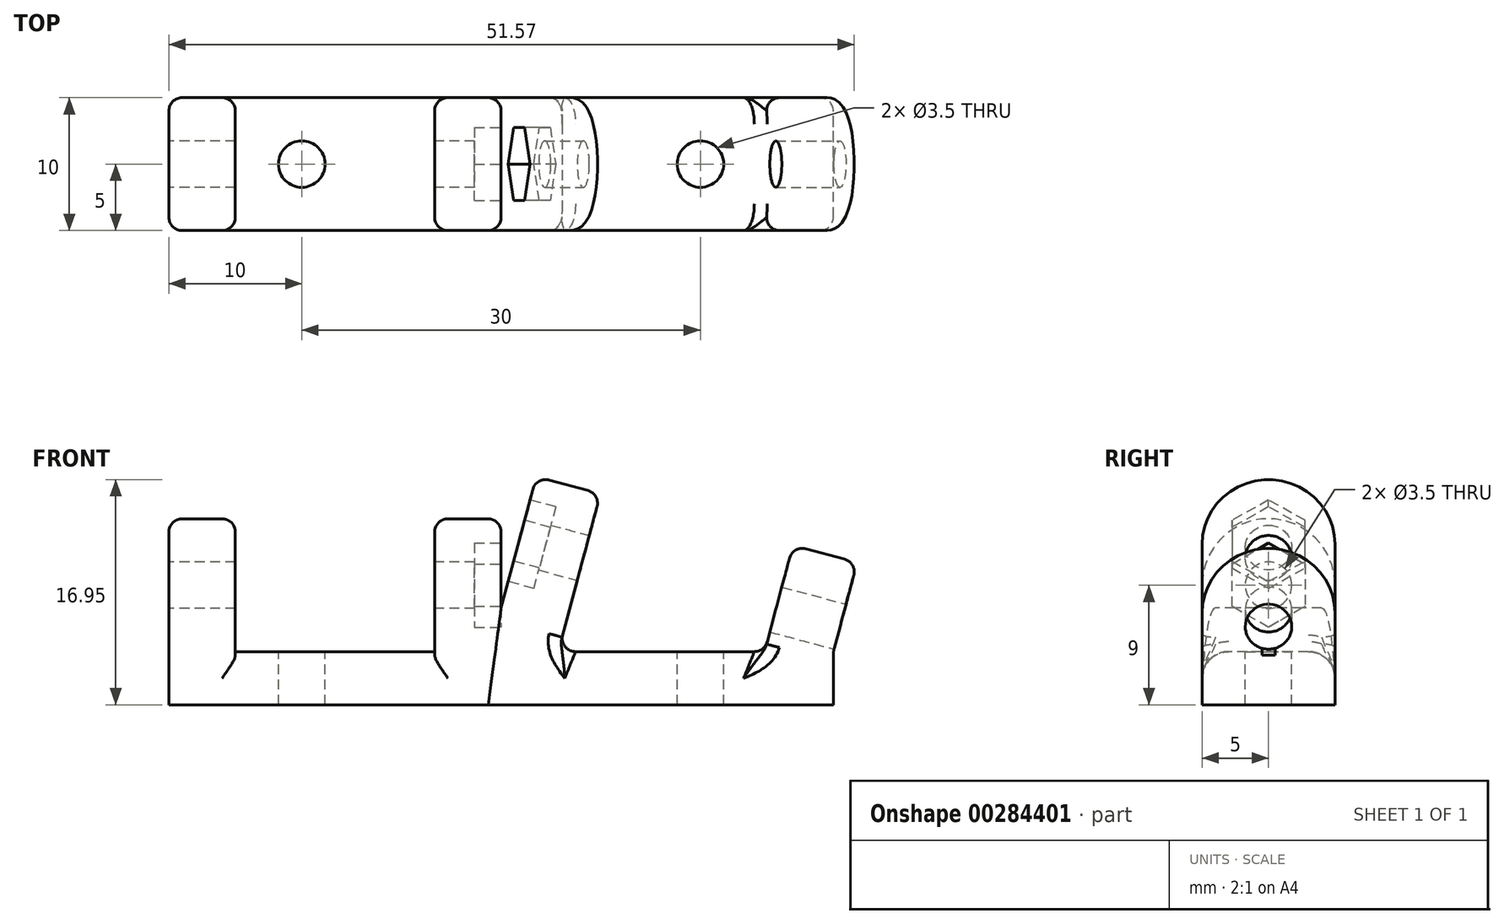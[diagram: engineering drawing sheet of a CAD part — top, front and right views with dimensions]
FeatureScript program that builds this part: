
annotation { "Feature Type Name" : "Feature", "Feature Type Description" : "" }
export const myFeature = defineFeature(function(context is Context, id is Id, definition is map)
    precondition{}
    {
        {
            var Q0;
            Q0=qCreatedBy(makeId("Top.planeOp"),FACE);
            var sketch = newSketch(context, id + "F0", { "sketchPlane" : qUnion([Q0])});
            skLineSegment(sketch, "E0.bottom", {"start": v(0, 0) * mm, "end": v(50, 0) * mm});
            skLineSegment(sketch, "E0.top", {"start": v(0, 10) * mm, "end": v(50, 10) * mm});
            skLineSegment(sketch, "E0.left", {"start": v(0, 0) * mm, "end": v(0, 10) * mm});
            skLineSegment(sketch, "E0.right", {"start": v(50, 0) * mm, "end": v(50, 10) * mm});
            skSolve(sketch);
        }
        {
            var Q0;
            Q0 = qSketchRegion(id + "F0", true);
            extrude(context, id + "F1", {"entities" : qUnion([Q0]), "depth" : 4 * mm});
        }
        {
            var Q0;
            Q0=makeQuery(id+"F1.opExtrude","SWEPT_FACE",FACE,{"disambiguationData":[OSD([sQuery(id+"F0.wireOp",EDGE,"E0.bottom")])]});
            var sketch = newSketch(context, id + "F2", { "sketchPlane" : qUnion([Q0])});
            skLineSegment(sketch, "E1", {"start": v(0, 4) * mm, "end": v(0, 14) * mm});
            skLineSegment(sketch, "E2", {"start": v(0, 14) * mm, "end": v(5, 14) * mm});
            skLineSegment(sketch, "E3", {"start": v(5, 14) * mm, "end": v(5, 4) * mm});
            skLineSegment(sketch, "E4", {"start": v(5, 4) * mm, "end": v(0, 4) * mm});
            skLineSegment(sketch, "E5", {"start": v(20, 4) * mm, "end": v(20, 14) * mm});
            skLineSegment(sketch, "E6", {"start": v(20, 14) * mm, "end": v(25, 14) * mm});
            skLineSegment(sketch, "E7", {"start": v(25, 14) * mm, "end": v(25, 7.3) * mm});
            skLineSegment(sketch, "E8", {"start": v(25, 4) * mm, "end": v(20, 4) * mm});
            skLineSegment(sketch, "E9", {"start": v(25, 7.3) * mm, "end": v(27.65, 17.18) * mm});
            skLineSegment(sketch, "E10", {"start": v(27.65, 17.18) * mm, "end": v(32.48, 15.88) * mm});
            skLineSegment(sketch, "E11", {"start": v(32.48, 15.88) * mm, "end": v(29.3, 4) * mm});
            skLineSegment(sketch, "E12", {"start": v(25, 4) * mm, "end": v(29.3, 4) * mm});
            skLineSegment(sketch, "E13", {"start": v(44.82, 4) * mm, "end": v(46.97, 12) * mm});
            skLineSegment(sketch, "E14", {"start": v(46.97, 12) * mm, "end": v(51.8, 10.7) * mm});
            skLineSegment(sketch, "E15", {"start": v(51.8, 10.7) * mm, "end": v(50, 4) * mm});
            skLineSegment(sketch, "E16", {"start": v(50, 4) * mm, "end": v(44.82, 4) * mm});
            skLineSegment(sketch, "E17", {"start": v(51.8, 10.7) * mm, "end": v(27.65, 17.18) * mm, "construction": true});
            skSolve(sketch);
        }
        {
            var Q0;
            Q0 = qSketchRegion(id + "F2", true);
            var Q1;
            Q1=makeQuery(id+"F1.opExtrude","SWEPT_FACE",FACE,{"disambiguationData":[OSD([sQuery(id+"F0.wireOp",EDGE,"E0.top")])]});
            extrude(context, id + "F3", {"entities" : qUnion([Q0]), "operationType" : NewBodyOperationType.ADD, "endBound" : BoundingType.UP_TO_SURFACE, "oppositeDirection" : true, "endBoundEntityFace" : qUnion([Q1]), "depth" : 25 * mm});
        }
        {
            var Q0;
            Q0=makeQuery(id+"F3.boolean.opBoolean","MERGE",FACE,{"derivedFrom":[makeQuery(id+"F1.opExtrude","SWEPT_FACE",FACE,{"disambiguationData":[OSD([sQuery(id+"F0.wireOp",EDGE,"E0.left")])]}),makeQuery(id+"F3.opExtrude","SWEPT_FACE",FACE,{"disambiguationData":[OSD([sQuery(id+"F2.wireOp",EDGE,"E1")])]})]});
            var sketch = newSketch(context, id + "F4", { "sketchPlane" : qUnion([Q0])});
            skCircle(sketch, "E18", {"center": v(-5, 9) * mm, "radius": 1.75 * mm});
            skPoint(sketch, "E18.centerSnap0", {"position": v(-5, 14) * mm});
            skSolve(sketch);
        }
        {
            var Q0;
            Q0 = qSketchRegion(id + "F4", true);
            var Q1;
            Q1=makeQuery(id+"F3.opExtrude","SWEPT_FACE",FACE,{"disambiguationData":[OSD([sQuery(id+"F2.wireOp",EDGE,"E7")])]});
            extrude(context, id + "F5", {"entities" : qUnion([Q0]), "operationType" : NewBodyOperationType.REMOVE, "endBound" : BoundingType.UP_TO_SURFACE, "oppositeDirection" : true, "endBoundEntityFace" : qUnion([Q1]), "depth" : 25 * mm});
        }
        {
            var Q0;
            Q0=makeQuery(id+"F3.opExtrude","SWEPT_FACE",FACE,{"disambiguationData":[OSD([sQuery(id+"F2.wireOp",EDGE,"E15")])]});
            var sketch = newSketch(context, id + "F6", { "sketchPlane" : qUnion([Q0])});
            skCircle(sketch, "E19", {"center": v(5, 18.75) * mm, "radius": 1.75 * mm});
            skPoint(sketch, "E19.centerSnap0", {"position": v(5, 23.75) * mm});
            skSolve(sketch);
        }
        {
            var Q0;
            Q0 = qSketchRegion(id + "F6", true);
            var Q1;
            Q1=makeQuery(id+"F3.opExtrude","SWEPT_FACE",FACE,{"disambiguationData":[OSD([sQuery(id+"F2.wireOp",EDGE,"E9")])]});
            extrude(context, id + "F7", {"entities" : qUnion([Q0]), "operationType" : NewBodyOperationType.REMOVE, "endBound" : BoundingType.UP_TO_SURFACE, "oppositeDirection" : true, "endBoundEntityFace" : qUnion([Q1]), "depth" : 25 * mm});
        }
        {
            var Q0;
            Q0=makeQuery(id+"F3.opExtrude","SWEPT_FACE",FACE,{"disambiguationData":[OSD([sQuery(id+"F2.wireOp",EDGE,"E9")])]});
            var sketch = newSketch(context, id + "F8", { "sketchPlane" : qUnion([Q0])});
            skCircle(sketch, "E20.cCircle", {"center": v(-5, 18.75) * mm, "radius": 2.75 * mm, "construction": true});
            skLineSegment(sketch, "E20.0", {"start": v(-2.25, 20.33) * mm, "end": v(-2.25, 17.16) * mm});
            skLineSegment(sketch, "E20.1", {"start": v(-2.25, 17.16) * mm, "end": v(-5, 15.57) * mm});
            skLineSegment(sketch, "E20.2", {"start": v(-5, 15.57) * mm, "end": v(-7.75, 17.16) * mm});
            skLineSegment(sketch, "E20.3", {"start": v(-7.75, 17.16) * mm, "end": v(-7.75, 20.33) * mm});
            skLineSegment(sketch, "E20.4", {"start": v(-7.75, 20.33) * mm, "end": v(-5, 21.92) * mm});
            skLineSegment(sketch, "E20.5", {"start": v(-5, 21.92) * mm, "end": v(-2.25, 20.33) * mm});
            skPoint(sketch, "E20.0.midPoint", {"position": v(-2.25, 18.75) * mm});
            skSolve(sketch);
        }
        {
            var Q0;
            Q0=makeQuery(id+"F3.opExtrude","SWEPT_FACE",FACE,{"disambiguationData":[OSD([sQuery(id+"F2.wireOp",EDGE,"E7")])]});
            var sketch = newSketch(context, id + "F9", { "sketchPlane" : qUnion([Q0])});
            skCircle(sketch, "E21.cCircle", {"center": v(5, 9) * mm, "radius": 2.75 * mm, "construction": true});
            skLineSegment(sketch, "E21.0", {"start": v(7.75, 10.59) * mm, "end": v(7.75, 7.41) * mm});
            skLineSegment(sketch, "E21.1", {"start": v(7.75, 7.41) * mm, "end": v(5, 5.82) * mm});
            skLineSegment(sketch, "E21.2", {"start": v(5, 5.82) * mm, "end": v(2.25, 7.41) * mm});
            skLineSegment(sketch, "E21.3", {"start": v(2.25, 7.41) * mm, "end": v(2.25, 10.59) * mm});
            skLineSegment(sketch, "E21.4", {"start": v(2.25, 10.59) * mm, "end": v(5, 12.18) * mm});
            skLineSegment(sketch, "E21.5", {"start": v(5, 12.18) * mm, "end": v(7.75, 10.59) * mm});
            skPoint(sketch, "E21.0.midPoint", {"position": v(7.75, 9) * mm});
            skSolve(sketch);
        }
        {
            var Q0;
            Q0 = qSketchRegion(id + "F8", true);
            extrude(context, id + "F10", {"entities" : qUnion([Q0]), "operationType" : NewBodyOperationType.REMOVE, "oppositeDirection" : true, "depth" : 2 * mm});
        }
        {
            var Q0;
            Q0 = qSketchRegion(id + "F9", true);
            extrude(context, id + "F11", {"entities" : qUnion([Q0]), "operationType" : NewBodyOperationType.REMOVE, "oppositeDirection" : true, "depth" : 2 * mm});
        }
        {
            var Q0;
            Q0=makeQuery(id+"F3.opExtrude","CAP_EDGE",EDGE,{"disambiguationData":[OSD([sQuery(id+"F2.wireOp",EDGE,"E2")])],"isStart":true});
            var Q1;
            Q1=makeQuery(id+"F3.opExtrude","CAP_EDGE",EDGE,{"disambiguationData":[OSD([sQuery(id+"F2.wireOp",EDGE,"E2")])],"isStart":false});
            var Q2;
            Q2=makeQuery(id+"F3.opExtrude","CAP_EDGE",EDGE,{"disambiguationData":[OSD([sQuery(id+"F2.wireOp",EDGE,"E6")])],"isStart":false});
            var Q3;
            Q3=makeQuery(id+"F3.opExtrude","CAP_EDGE",EDGE,{"disambiguationData":[OSD([sQuery(id+"F2.wireOp",EDGE,"E6")])],"isStart":true});
            var Q4;
            Q4=makeQuery(id+"F3.opExtrude","CAP_EDGE",EDGE,{"disambiguationData":[OSD([sQuery(id+"F2.wireOp",EDGE,"E10")])],"isStart":false});
            var Q5;
            Q5=makeQuery(id+"F3.opExtrude","CAP_EDGE",EDGE,{"disambiguationData":[OSD([sQuery(id+"F2.wireOp",EDGE,"E10")])],"isStart":true});
            var Q6;
            Q6=makeQuery(id+"F3.opExtrude","CAP_EDGE",EDGE,{"disambiguationData":[OSD([sQuery(id+"F2.wireOp",EDGE,"E14")])],"isStart":false});
            var Q7;
            Q7=makeQuery(id+"F3.opExtrude","CAP_EDGE",EDGE,{"disambiguationData":[OSD([sQuery(id+"F2.wireOp",EDGE,"E14")])],"isStart":true});
            fillet(context, id + "F12", {"entities" : qUnion([Q0, Q1, Q2, Q3, Q4, Q5, Q6, Q7]), "radius" : 5 * mm, "tangentPropagation" : true, "allowEdgeOverflow" : false});
        }
        {
            var Q0;
            {var subQ1=sQuery(id+"F2.wireOp",EDGE,"E3");var subQ4=sQuery(id+"F0.wireOp",EDGE,"E0.top");var subQ5=sQuery(id+"F0.wireOp",EDGE,"E0.bottom");Q0=makeQuery(id+"F3.boolean.opBoolean","SPLIT",FACE,{"disambiguationData":[TD([makeQuery(id+"F3.opExtrude","SWEPT_FACE",FACE,{"disambiguationData":[OSD([subQ1])]})])],"derivedFrom":makeQuery(id+"F1.opExtrude","CAP_FACE",FACE,{"disambiguationData":[OSD([subQ5,subQ4,sQuery(id+"F0.wireOp",EDGE,"E0.left"),sQuery(id+"F0.wireOp",EDGE,"E0.right")])],"isStart":false})});}
            var sketch = newSketch(context, id + "F13", { "sketchPlane" : qUnion([Q0])});
            skCircle(sketch, "E22", {"center": v(10, 5) * mm, "radius": 1.75 * mm});
            skPoint(sketch, "E22.centerSnap0", {"position": v(5, 5) * mm});
            skCircle(sketch, "E23", {"center": v(40, 5) * mm, "radius": 1.75 * mm});
            skSolve(sketch);
        }
        {
            var Q0;
            Q0 = qSketchRegion(id + "F13", true);
            extrude(context, id + "F14", {"entities" : qUnion([Q0]), "operationType" : NewBodyOperationType.REMOVE, "endBound" : BoundingType.THROUGH_ALL, "oppositeDirection" : true, "depth" : 25 * mm});
        }
        {
            var Q0;
            {var subQ0=sQuery(id+"F2.wireOp",EDGE,"E3");var subQ1=sQuery(id+"F0.wireOp",EDGE,"E0.top");Q0=makeQuery(id+"F3.boolean.opBoolean","SPLIT",EDGE,{"disambiguationData":[TD([makeQuery(id+"F3.opExtrude","SWEPT_FACE",FACE,{"disambiguationData":[OSD([subQ0])]})])],"derivedFrom":makeQuery(id+"F1.opExtrude","CAP_EDGE",EDGE,{"disambiguationData":[OSD([subQ1])],"isStart":false})});}
            var Q1;
            {var subQ0=sQuery(id+"F2.wireOp",EDGE,"E3");var subQ1=sQuery(id+"F0.wireOp",EDGE,"E0.bottom");Q1=makeQuery(id+"F3.boolean.opBoolean","SPLIT",EDGE,{"disambiguationData":[TD([makeQuery(id+"F3.opExtrude","SWEPT_FACE",FACE,{"disambiguationData":[OSD([subQ0])]})])],"derivedFrom":makeQuery(id+"F1.opExtrude","CAP_EDGE",EDGE,{"disambiguationData":[OSD([subQ1])],"isStart":false})});}
            var Q2;
            {var subQ0=sQuery(id+"F2.wireOp",EDGE,"E11");var subQ1=sQuery(id+"F0.wireOp",EDGE,"E0.top");Q2=makeQuery(id+"F3.boolean.opBoolean","SPLIT",EDGE,{"disambiguationData":[TD([makeQuery(id+"F3.opExtrude","SWEPT_FACE",FACE,{"disambiguationData":[OSD([subQ0])]})])],"derivedFrom":makeQuery(id+"F1.opExtrude","CAP_EDGE",EDGE,{"disambiguationData":[OSD([subQ1])],"isStart":false})});}
            var Q3;
            {var subQ0=sQuery(id+"F0.wireOp",EDGE,"E0.bottom");var subQ1=sQuery(id+"F2.wireOp",EDGE,"E11");Q3=makeQuery(id+"F3.boolean.opBoolean","SPLIT",EDGE,{"disambiguationData":[TD([makeQuery(id+"F3.opExtrude","SWEPT_FACE",FACE,{"disambiguationData":[OSD([subQ1])]})])],"derivedFrom":makeQuery(id+"F1.opExtrude","CAP_EDGE",EDGE,{"disambiguationData":[OSD([subQ0])],"isStart":false})});}
            var Q4;
            {var subQ0=sQuery(id+"F2.wireOp",EDGE,"E7");var subQ2=sQuery(id+"F0.wireOp",EDGE,"E0.top");Q4=makeQuery(id+"F3.boolean.opBoolean","SPLIT",EDGE,{"disambiguationData":[TD([makeQuery(id+"F3.opExtrude","SWEPT_FACE",FACE,{"disambiguationData":[OSD([subQ0])]})])],"derivedFrom":makeQuery(id+"F1.opExtrude","CAP_EDGE",EDGE,{"disambiguationData":[OSD([subQ2])],"isStart":false})});}
            var Q5;
            {var subQ0=sQuery(id+"F2.wireOp",EDGE,"E7");var subQ1=sQuery(id+"F0.wireOp",EDGE,"E0.bottom");Q5=makeQuery(id+"F3.boolean.opBoolean","SPLIT",EDGE,{"disambiguationData":[TD([makeQuery(id+"F3.opExtrude","SWEPT_FACE",FACE,{"disambiguationData":[OSD([subQ0])]})])],"derivedFrom":makeQuery(id+"F1.opExtrude","CAP_EDGE",EDGE,{"disambiguationData":[OSD([subQ1])],"isStart":false})});}
            fillet(context, id + "F15", {"entities" : qUnion([Q0, Q1, Q2, Q3, Q4, Q5]), "radius" : 2 * mm, "tangentPropagation" : true, "allowEdgeOverflow" : false});
        }
        {
            var Q0;
            Q0=makeQuery(id+"F3.opExtrude","SWEPT_EDGE",EDGE,{"disambiguationData":[OSD([sQuery(id+"F0.wireOp",EDGE,"E0.bottom"),sQuery(id+"F2.wireOp",EDGE,"E11"),sQuery(id+"F2.wireOp",EDGE,"E12")])]});
            var Q1;
            Q1=makeQuery(id+"F3.opExtrude","SWEPT_EDGE",EDGE,{"disambiguationData":[OSD([sQuery(id+"F0.wireOp",EDGE,"E0.bottom"),sQuery(id+"F2.wireOp",EDGE,"E5"),sQuery(id+"F2.wireOp",EDGE,"E8")])]});
            var Q2;
            Q2=makeQuery(id+"F3.opExtrude","SWEPT_EDGE",EDGE,{"disambiguationData":[OSD([sQuery(id+"F0.wireOp",EDGE,"E0.bottom"),sQuery(id+"F2.wireOp",EDGE,"E3"),sQuery(id+"F2.wireOp",EDGE,"E4")])]});
            var Q3;
            Q3=makeQuery(id+"F3.opExtrude","SWEPT_EDGE",EDGE,{"disambiguationData":[OSD([sQuery(id+"F0.wireOp",EDGE,"E0.bottom"),sQuery(id+"F2.wireOp",EDGE,"E5"),sQuery(id+"F2.wireOp",EDGE,"E8")])]});
            var Q4;
            Q4=makeQuery(id+"F3.opExtrude","SWEPT_EDGE",EDGE,{"disambiguationData":[OSD([sQuery(id+"F0.wireOp",EDGE,"E0.bottom"),sQuery(id+"F2.wireOp",EDGE,"E11"),sQuery(id+"F2.wireOp",EDGE,"E12")])]});
            var Q5;
            Q5=makeQuery(id+"F3.opExtrude","SWEPT_EDGE",EDGE,{"disambiguationData":[OSD([sQuery(id+"F0.wireOp",EDGE,"E0.bottom"),sQuery(id+"F2.wireOp",EDGE,"E13"),sQuery(id+"F2.wireOp",EDGE,"E16")])]});
            fillet(context, id + "F16", {"entities" : qUnion([Q0, Q1, Q2, Q3, Q4, Q5]), "radius" : 1 * mm, "tangentPropagation" : true, "allowEdgeOverflow" : false});
        }
        {
            var Q0;
            Q0=makeQuery(id+"F3.opExtrude","CAP_EDGE",EDGE,{"disambiguationData":[OSD([sQuery(id+"F2.wireOp",EDGE,"E5")])],"isStart":true});
            var Q1;
            Q1=makeQuery(id+"F12.opFillet","BLEND_EDGE",EDGE,{"blendedFrom":[makeQuery(id+"F3.opExtrude","CAP_EDGE",EDGE,{"disambiguationData":[OSD([sQuery(id+"F2.wireOp",EDGE,"E6")])],"isStart":true}),makeQuery(id+"F3.opExtrude","SWEPT_FACE",FACE,{"disambiguationData":[OSD([sQuery(id+"F2.wireOp",EDGE,"E7")])]})],"blendedInto":[makeQuery(id+"F3.opExtrude","SWEPT_FACE",FACE,{"disambiguationData":[OSD([sQuery(id+"F2.wireOp",EDGE,"E7")])]})]});
            var Q2;
            Q2=makeQuery(id+"F12.opFillet","BLEND_EDGE",EDGE,{"blendedFrom":[makeQuery(id+"F3.opExtrude","CAP_EDGE",EDGE,{"disambiguationData":[OSD([sQuery(id+"F2.wireOp",EDGE,"E2")])],"isStart":true}),makeQuery(id+"F3.boolean.opBoolean","MERGE",FACE,{"derivedFrom":[makeQuery(id+"F1.opExtrude","SWEPT_FACE",FACE,{"disambiguationData":[OSD([sQuery(id+"F0.wireOp",EDGE,"E0.left")])]}),makeQuery(id+"F3.opExtrude","SWEPT_FACE",FACE,{"disambiguationData":[OSD([sQuery(id+"F2.wireOp",EDGE,"E1")])]})]})],"blendedInto":[makeQuery(id+"F3.boolean.opBoolean","MERGE",FACE,{"derivedFrom":[makeQuery(id+"F1.opExtrude","SWEPT_FACE",FACE,{"disambiguationData":[OSD([sQuery(id+"F0.wireOp",EDGE,"E0.left")])]}),makeQuery(id+"F3.opExtrude","SWEPT_FACE",FACE,{"disambiguationData":[OSD([sQuery(id+"F2.wireOp",EDGE,"E1")])]})]})]});
            var Q3;
            Q3=makeQuery(id+"F12.opFillet","BLEND_EDGE",EDGE,{"blendedFrom":[makeQuery(id+"F3.opExtrude","CAP_EDGE",EDGE,{"disambiguationData":[OSD([sQuery(id+"F2.wireOp",EDGE,"E2")])],"isStart":true}),makeQuery(id+"F3.opExtrude","SWEPT_FACE",FACE,{"disambiguationData":[OSD([sQuery(id+"F2.wireOp",EDGE,"E3")])]})],"blendedInto":[makeQuery(id+"F3.opExtrude","SWEPT_FACE",FACE,{"disambiguationData":[OSD([sQuery(id+"F2.wireOp",EDGE,"E3")])]})]});
            var Q4;
            Q4=makeQuery(id+"F12.opFillet","BLEND_EDGE",EDGE,{"blendedFrom":[makeQuery(id+"F3.opExtrude","CAP_EDGE",EDGE,{"disambiguationData":[OSD([sQuery(id+"F2.wireOp",EDGE,"E10")])],"isStart":true}),makeQuery(id+"F3.opExtrude","SWEPT_FACE",FACE,{"disambiguationData":[OSD([sQuery(id+"F2.wireOp",EDGE,"E9")])]})],"blendedInto":[makeQuery(id+"F3.opExtrude","SWEPT_FACE",FACE,{"disambiguationData":[OSD([sQuery(id+"F2.wireOp",EDGE,"E9")])]})]});
            var Q5;
            Q5=makeQuery(id+"F12.opFillet","BLEND_EDGE",EDGE,{"blendedFrom":[makeQuery(id+"F3.opExtrude","CAP_EDGE",EDGE,{"disambiguationData":[OSD([sQuery(id+"F2.wireOp",EDGE,"E10")])],"isStart":true}),makeQuery(id+"F3.opExtrude","SWEPT_FACE",FACE,{"disambiguationData":[OSD([sQuery(id+"F2.wireOp",EDGE,"E11")])]})],"blendedInto":[makeQuery(id+"F3.opExtrude","SWEPT_FACE",FACE,{"disambiguationData":[OSD([sQuery(id+"F2.wireOp",EDGE,"E11")])]})]});
            var Q6;
            Q6=makeQuery(id+"F12.opFillet","BLEND_EDGE",EDGE,{"blendedFrom":[makeQuery(id+"F3.opExtrude","CAP_EDGE",EDGE,{"disambiguationData":[OSD([sQuery(id+"F2.wireOp",EDGE,"E14")])],"isStart":true}),makeQuery(id+"F3.opExtrude","SWEPT_FACE",FACE,{"disambiguationData":[OSD([sQuery(id+"F2.wireOp",EDGE,"E13")])]})],"blendedInto":[makeQuery(id+"F3.opExtrude","SWEPT_FACE",FACE,{"disambiguationData":[OSD([sQuery(id+"F2.wireOp",EDGE,"E13")])]})]});
            fillet(context, id + "F17", {"entities" : qUnion([Q0, Q1, Q2, Q3, Q4, Q5, Q6]), "radius" : 1 * mm, "tangentPropagation" : true, "allowEdgeOverflow" : false});
        }
        {
            var Q0;
            {var subQ0=sQuery(id+"F0.wireOp",EDGE,"E0.right");Q0=makeQuery(id+"F3.boolean.opBoolean","MERGE",EDGE,{"derivedFrom":[makeQuery(id+"F1.opExtrude","CAP_EDGE",EDGE,{"disambiguationData":[OSD([subQ0])],"isStart":false}),makeQuery(id+"F3.opExtrude","SWEPT_EDGE",EDGE,{"disambiguationData":[OSD([sQuery(id+"F0.wireOp",EDGE,"E0.bottom"),subQ0,sQuery(id+"F2.wireOp",EDGE,"E15"),sQuery(id+"F2.wireOp",EDGE,"E16")])]})]});}
            fillet(context, id + "F18", {"entities" : qUnion([Q0]), "radius" : 2 * mm, "tangentPropagation" : true, "allowEdgeOverflow" : false});
        }
        {
            var Q0;
            Q0=makeQuery(id+"F12.opFillet","BLEND_EDGE",EDGE,{"blendedFrom":[makeQuery(id+"F3.opExtrude","CAP_EDGE",EDGE,{"disambiguationData":[OSD([sQuery(id+"F2.wireOp",EDGE,"E14")])],"isStart":true}),makeQuery(id+"F3.opExtrude","SWEPT_FACE",FACE,{"disambiguationData":[OSD([sQuery(id+"F2.wireOp",EDGE,"E15")])]})],"blendedInto":[makeQuery(id+"F3.opExtrude","SWEPT_FACE",FACE,{"disambiguationData":[OSD([sQuery(id+"F2.wireOp",EDGE,"E15")])]})]});
            fillet(context, id + "F19", {"entities" : qUnion([Q0]), "radius" : 1 * mm, "tangentPropagation" : true, "allowEdgeOverflow" : false});
        }
    });
